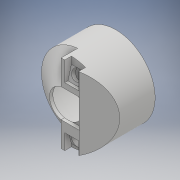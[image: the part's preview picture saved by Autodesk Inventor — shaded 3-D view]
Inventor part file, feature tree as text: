
AUTODESK INVENTOR PART (.ipt)
format: ipt  version: 2019 (Build 230136000, 136)  size: 251,904 bytes
history: native  units: mm
features: sketch x15, extrude x13, revolve x2, plane x2
ambient origin geometry x8: Origin, YZ Plane, XZ Plane, XY Plane, X Axis, Y Axis, Z Axis, Center Point
bodies: Solid1 (feature_tree)
feature tree (32):
  extrude  "Extrusion-Main-Body"  Depth=25.0mm TaperAngle=0.0deg
  extrude  "Extrusion-Inner-Cylinder"  Depth=25.0mm TaperAngle=0.0deg
  revolve  "Revolution1"  [1 undecoded]
  extrude  "Extrusion-Clamp-L"  Depth=6.8mm
  extrude  "Extrusion-Clamp-R"  Depth=3.7mm
  extrude  "Extrusion-Back-Face"  Depth=6.8mm
  revolve  "Revolution-Front-Face"  [1 undecoded]
  plane  "Work Plane1"
  extrude  "Extrusion-Clamp-Support-L"  Depth=3.2mm TaperAngle=0.0deg
  plane  "Work Plane2"
  extrude  "Extrusion-Clamp-Support-R"  Depth=25.481807mm
  sketch  "Sketch14"  dims[d35=180.0deg d37=19.0mm]
  extrude  "Extrusion14"  Depth=19.0mm
  extrude  "Extrusion-Clamp-Chamfer-L"  Depth=4.0mm TaperAngle=0.0deg
  extrude  "Extrusion-Clamp-Chamfer-R"  Depth=4.0mm TaperAngle=0.0deg
  extrude  "Extrusion-Magnet-L"  Depth=6.1mm
  extrude  "Extrusion-Magnet-R"  Depth=7.0mm TaperAngle=0.0deg
  extrude  "Extrusion-Headbar-Top"  Depth=5.1mm
  sketch  "Sketch1"  dims[d0=38.0mm d1=25.0mm d2=0.0mm]
  sketch  "Sketch2"  dims[d3=9.4mm d4=25.0mm d5=0.0mm]
  sketch  "Sketch3"  dims[d6=15.5mm d7=25.481807mm]
  sketch  "Sketch4"  dims[d8=90.0deg d9=6.8mm]
  sketch  "Sketch5"  dims[d10=9.5mm d12=3.7mm]
  sketch  "Sketch8"  dims[d13=3.2mm d14=0.0mm d15=6.8mm]
  sketch  "Sketch9"  dims[d16=10.0mm d17=11.5mm]
  sketch  "Sketch11"  dims[d18=3.7mm d19=3.2mm d20=0.0mm]
  sketch  "Sketch12"  dims[d32=4.0mm d33=0.0mm d34=25.481807mm]
  sketch  "Sketch15"  dims[d38=1.5mm d39=4.0mm d40=0.0mm]
  sketch  "Sketch19"  dims[d41=-19.0mm d42=4.0mm d43=0.0mm]
  sketch  "Sketch21"  dims[d44=5.934119mm d54=6.1mm]
  sketch  "Sketch23"  dims[d55=1.7mm d56=7.0mm d57=0.0mm]
  sketch  "Sketch24"  dims[d58=25.0mm d59=0.0mm d66=5.1mm d67=2.0mm d68=0.0mm d73=3.4mm d76=3.8mm d78=1.75mm d79=0.0mm d83=6.1mm d84=1.7mm d85=90.0deg d86=6.8mm d87=0.0mm d88=5.1mm d89=3.4mm d90=3.8mm d91=2.0mm d92=0.0mm]
note: 2 required parameter values undecoded (feature->parameter linkage not recoverable at this tier; creation-order binding heuristic only, values carry confidence <= 0.55)
